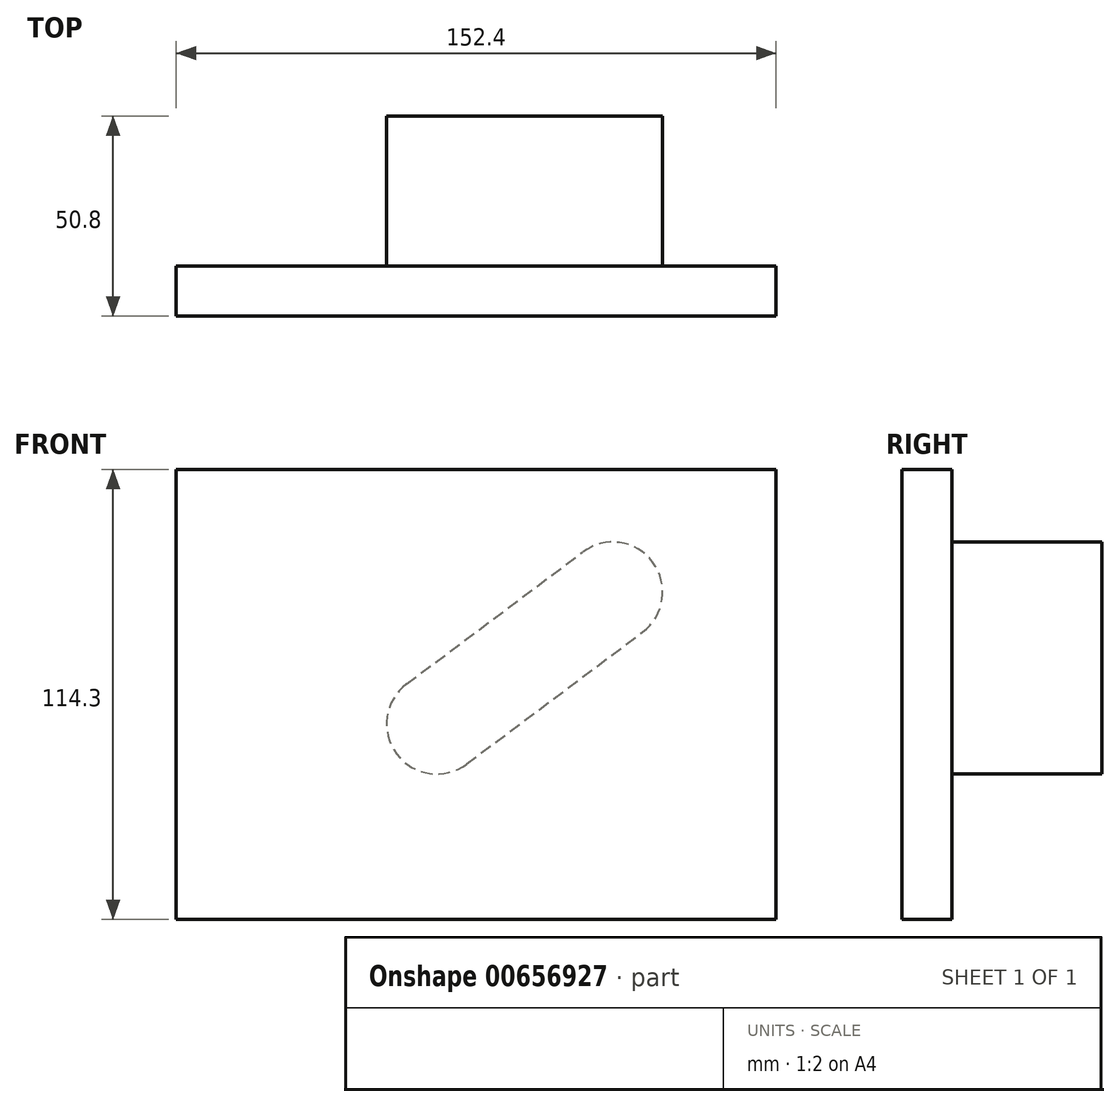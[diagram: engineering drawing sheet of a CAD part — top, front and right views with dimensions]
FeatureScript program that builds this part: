
annotation { "Feature Type Name" : "Feature", "Feature Type Description" : "" }
export const myFeature = defineFeature(function(context is Context, id is Id, definition is map)
    precondition{}
    {
        {
            var Q0;
            Q0=qCreatedBy(makeId("Front.planeOp"),FACE);
            var sketch = newSketch(context, id + "F0", { "sketchPlane" : qUnion([Q0])});
            skLineSegment(sketch, "E0.bottom", {"start": v(-76.2, 57.15) * mm, "end": v(76.2, 57.15) * mm});
            skLineSegment(sketch, "E0.top", {"start": v(-76.2, -57.15) * mm, "end": v(76.2, -57.15) * mm});
            skLineSegment(sketch, "E0.left", {"start": v(-76.2, 57.15) * mm, "end": v(-76.2, -57.15) * mm});
            skLineSegment(sketch, "E0.right", {"start": v(76.2, 57.15) * mm, "end": v(76.2, -57.15) * mm});
            skPoint(sketch, "E0.middle", {"position": v(0, 0) * mm});
            skSolve(sketch);
        }
        {
            var Q0;
            Q0=makeQuery(id+"F0.imprint","IMPRINT",FACE,{"disambiguationData":[TD([[makeQuery(id+"F0.imprint","IMPRINT",EDGE,{"derivedFrom":sQuery(id+"F0.wireOp",EDGE,"E0.bottom")}),-1.0]])]});
            extrude(context, id + "F1", {"entities" : qUnion([Q0]), "depth" : 12.7 * mm, "offsetDistance" : 25.4 * mm});
        }
        {
            var Q0;
            Q0=makeQuery(id+"F1.opExtrude","CAP_FACE",FACE,{"disambiguationData":[OSD([sQuery(id+"F0.wireOp",EDGE,"E0.bottom"),sQuery(id+"F0.wireOp",EDGE,"E0.top"),sQuery(id+"F0.wireOp",EDGE,"E0.left"),sQuery(id+"F0.wireOp",EDGE,"E0.right")])],"isStart":true});
            var sketch = newSketch(context, id + "F2", { "sketchPlane" : qUnion([Q0])});
            skLineSegment(sketch, "E1", {"start": v(76.2, -57.15) * mm, "end": v(-76.2, 57.15) * mm, "construction": true});
            skLineSegment(sketch, "E2", {"start": v(2.4, -17.68) * mm, "end": v(-42.3, 15.85) * mm});
            skLineSegment(sketch, "E3", {"start": v(17.64, 2.64) * mm, "end": v(-27.06, 36.17) * mm});
            skLineSegment(sketch, "E4", {"start": v(0, 0) * mm, "end": v(7.62, 10.16) * mm, "construction": true});
            skLineSegment(sketch, "E5", {"start": v(0, 0) * mm, "end": v(-7.62, -10.16) * mm, "construction": true});
            skArc(sketch, "E6", {"start": v(2.4, -17.68) * mm, "mid": v(20.18, -15.14) * mm, "end": v(17.64, 2.64) * mm});
            skArc(sketch, "E7", {"start": v(-27.06, 36.17) * mm, "mid": v(-44.84, 33.63) * mm, "end": v(-42.3, 15.85) * mm});
            skSolve(sketch);
        }
        {
            var Q0;
            Q0 = qSketchRegion(id + "F2", true);
            extrude(context, id + "F3", {"entities" : qUnion([Q0]), "operationType" : NewBodyOperationType.ADD, "depth" : 38.1 * mm, "offsetDistance" : 25.4 * mm});
        }
    });
